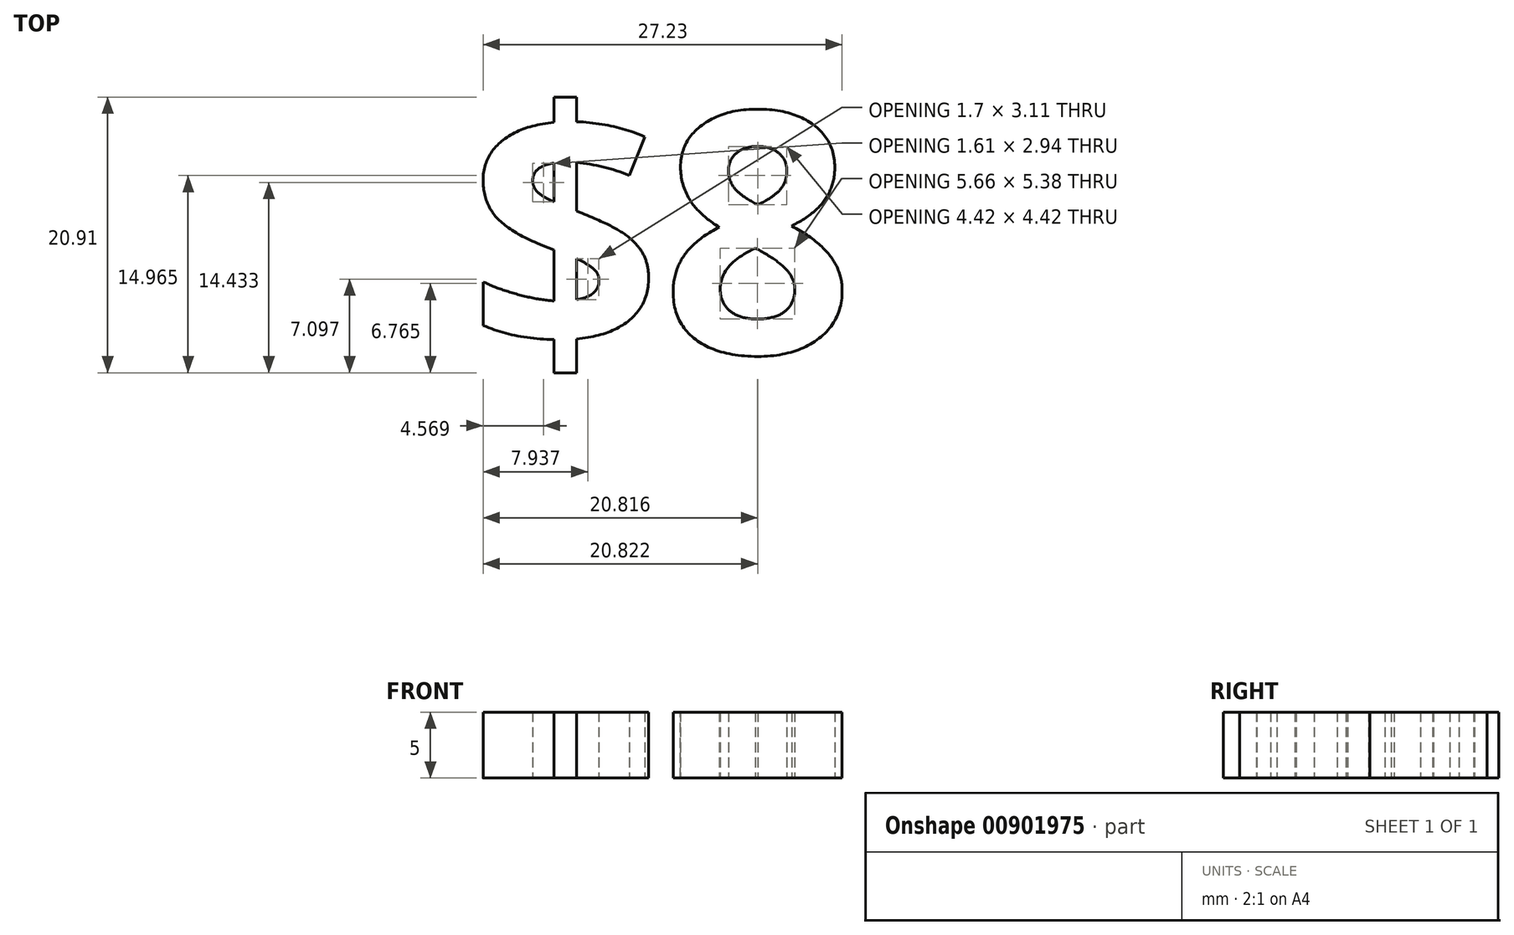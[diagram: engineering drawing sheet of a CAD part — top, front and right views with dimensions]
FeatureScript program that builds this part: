
annotation { "Feature Type Name" : "Feature", "Feature Type Description" : "" }
export const myFeature = defineFeature(function(context is Context, id is Id, definition is map)
    precondition{}
    {
        {
            var Q0;
            Q0=qCreatedBy(makeId("Top.planeOp"),FACE);
            var sketch = newSketch(context, id + "F0", { "sketchPlane" : qUnion([Q0])});
            skText(sketch, "E0", { "text": "$8", "fontName": "OpenSans-Bold.ttf"});
            const initialGuessF0  = {"E0": [-0.015, -0.009, 1, 0, 0.01843]};
            skSetInitialGuess(sketch, initialGuessF0);
            skSolve(sketch);
        }
        {
            var Q0;
            Q0=makeQuery(id+"F0.imprint","IMPRINT",FACE,{"disambiguationData":[TD([[makeQuery(id+"F0.imprint","IMPRINT",EDGE,{"derivedFrom":sQuery(id+"F0.wireOp",EDGE,"E0.sketch_text.stroke-0")}),-1.0]])]});
            var Q1;
            Q1=makeQuery(id+"F0.imprint","IMPRINT",FACE,{"disambiguationData":[TD([[makeQuery(id+"F0.imprint","IMPRINT",EDGE,{"derivedFrom":sQuery(id+"F0.wireOp",EDGE,"E0.sketch_text.stroke-33")}),-1.0]])]});
            extrude(context, id + "F1", {"entities" : qUnion([Q0, Q1]), "depth" : 5 * mm, "offsetDistance" : 25 * mm});
        }
    });
